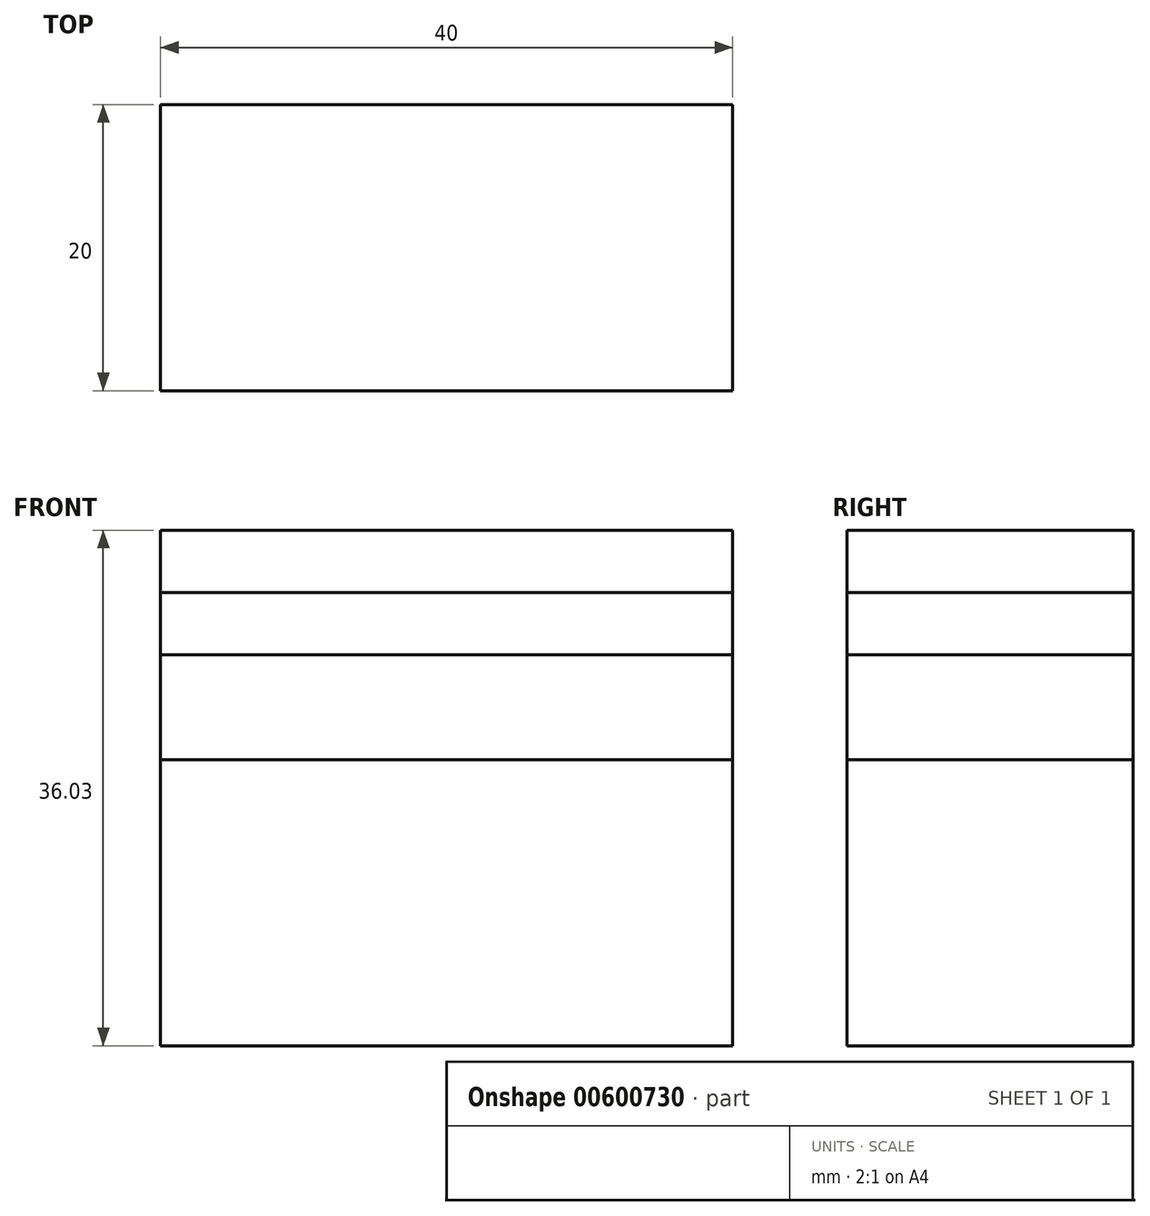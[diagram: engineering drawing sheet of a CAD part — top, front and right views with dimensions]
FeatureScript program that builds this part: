
annotation { "Feature Type Name" : "Feature", "Feature Type Description" : "" }
export const myFeature = defineFeature(function(context is Context, id is Id, definition is map)
    precondition{}
    {
        {
            var Q0;
            Q0=qCreatedBy(makeId("Front.planeOp"),FACE);
            var sketch = newSketch(context, id + "F0", { "sketchPlane" : qUnion([Q0])});
            skLineSegment(sketch, "E0", {"start": v(0, 0) * mm, "end": v(0, -20) * mm, "construction": true});
            skLineSegment(sketch, "E1", {"start": v(0, -20) * mm, "end": v(-20, -20) * mm});
            skLineSegment(sketch, "E2", {"start": v(-20, -20) * mm, "end": v(-20, 0) * mm});
            skLineSegment(sketch, "E3", {"start": v(-20, 0) * mm, "end": v(-20, 7.31) * mm});
            skLineSegment(sketch, "E4", {"start": v(-20, 7.31) * mm, "end": v(-20, 11.67) * mm});
            skLineSegment(sketch, "E5", {"start": v(-20, 11.67) * mm, "end": v(-20, 16.03) * mm});
            skLineSegment(sketch, "E6", {"start": v(-20, 16.03) * mm, "end": v(20, 16.03) * mm});
            skLineSegment(sketch, "E7", {"start": v(20, 16.03) * mm, "end": v(20, -20) * mm});
            skLineSegment(sketch, "E8", {"start": v(20, -20) * mm, "end": v(0, -20) * mm});
            skLineSegment(sketch, "E9", {"start": v(-20, 0) * mm, "end": v(20, 0) * mm});
            skLineSegment(sketch, "E10", {"start": v(-20, 7.31) * mm, "end": v(20, 7.31) * mm});
            skLineSegment(sketch, "E11", {"start": v(-20, 11.67) * mm, "end": v(20, 11.67) * mm});
            skSolve(sketch);
        }
        {
            var Q0;
            Q0=makeQuery(id+"F0.imprint","IMPRINT",FACE,{"disambiguationData":[TD([[makeQuery(id+"F0.imprint","IMPRINT",EDGE,{"derivedFrom":sQuery(id+"F0.wireOp",EDGE,"E1")}),-1.0]])]});
            extrude(context, id + "F1", {"entities" : qUnion([Q0]), "depth" : 20 * mm, "offsetDistance" : 25 * mm});
        }
        {
            var Q0;
            Q0=makeQuery(id+"F0.imprint","IMPRINT",FACE,{"disambiguationData":[TD([[makeQuery(id+"F0.imprint","IMPRINT",EDGE,{"derivedFrom":sQuery(id+"F0.wireOp",EDGE,"E3")}),-1.0]])]});
            extrude(context, id + "F2", {"entities" : qUnion([Q0]), "depth" : 20 * mm, "offsetDistance" : 25 * mm});
        }
        {
            var Q0;
            Q0=makeQuery(id+"F0.imprint","IMPRINT",FACE,{"disambiguationData":[TD([[makeQuery(id+"F0.imprint","IMPRINT",EDGE,{"derivedFrom":sQuery(id+"F0.wireOp",EDGE,"E4")}),-1.0]])]});
            extrude(context, id + "F3", {"entities" : qUnion([Q0]), "depth" : 20 * mm, "offsetDistance" : 25 * mm});
        }
        {
            var Q0;
            Q0=makeQuery(id+"F0.imprint","IMPRINT",FACE,{"disambiguationData":[TD([[makeQuery(id+"F0.imprint","IMPRINT",EDGE,{"derivedFrom":sQuery(id+"F0.wireOp",EDGE,"E5")}),-1.0]])]});
            extrude(context, id + "F4", {"entities" : qUnion([Q0]), "depth" : 20 * mm, "offsetDistance" : 25 * mm});
        }
    });
